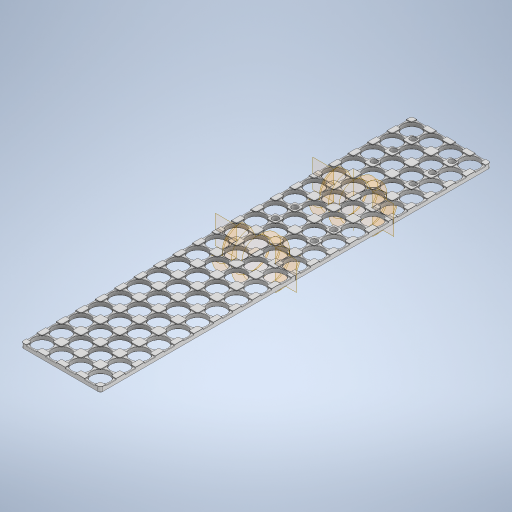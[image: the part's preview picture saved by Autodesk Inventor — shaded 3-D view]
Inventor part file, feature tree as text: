
AUTODESK INVENTOR PART (.ipt)
format: ipt  version: 2024.2 (Build 282272000, 272)  size: 6,418,944 bytes
history: native  units: mm
features: other x22, surface_op x13, chamfer x9, revolve x7, thicken_offset x6, pattern_linear x5, sketch x5, extrude x3, fillet x3, hole x2, split x2, pattern_circular x1
ambient origin geometry x8: Origin, YZ Plane, XZ Plane, XY Plane, X Axis, Y Axis, Z Axis, Center Point
bodies: Solid1 (feature_tree), Solid2 (feature_tree), Solid4 (feature_tree)
feature tree (78):
  extrude  "Extrusion1"  Depth=23.5mm
  extrude  "Extrusion2"  Depth=5.5mm TaperAngle=0.0deg
  fillet  "Fillet1"  Radius=5.5mm
  chamfer  "Chamfer1"  Distance=1.0mm
  chamfer  "Chamfer2"  Distance=0.4mm Angle=45.0deg
  pattern_linear  "Rectangular Pattern1"  Count1=4 Spacing1=23.5mm
  sketch  "Sketch3"  dims[d6=5.5mm d7=1.0mm d8=0.0mm]
  surface_op  "Stitch Surface1"
  other  "Work Axis1"
  pattern_circular  "Circular Pattern1"  Count=20  [1 undecoded]
  surface_op  "Extend3"
  surface_op  "Extend4"
  surface_op  "Stitch Surface8"
  pattern_linear  "Rectangular Pattern2"  Spacing1=23.5mm  [1 undecoded]
  hole  "Hole1"  [1 undecoded]
  chamfer  "Chamfer3"  Distance=23.5mm
  hole  "Hole2"  [1 undecoded]
  chamfer  "Chamfer4"  Distance=13.0mm
  pattern_linear  "Rectangular Pattern4"  Count1=2 Spacing1=23.5mm
  pattern_linear  "Rectangular Pattern5"  Spacing1=10.0mm  [1 undecoded]
  chamfer  "Chamfer5"  Distance=23.5mm
  chamfer  "Chamfer6"  Angle=180.0deg  [1 undecoded]
  thicken_offset  "Thicken8"
  fillet  "Fillet2"  [1 undecoded]
  chamfer  "Chamfer7"  Angle=180.0deg  [1 undecoded]
  chamfer  "Chamfer8"  Angle=180.0deg  [1 undecoded]
  chamfer  "Chamfer9"  Angle=90.0deg  [1 undecoded]
  split  "Split1"
  thicken_offset  "Thicken3"
  thicken_offset  "Thicken4"
  pattern_linear  "Rectangular Pattern6"  Spacing1=90.0deg  [1 undecoded]
  surface_op  "Stitch Surface11"
  split  "Split2"
  thicken_offset  "Thicken5"
  thicken_offset  "Thicken6"
  thicken_offset  "Thicken7"
  fillet  "Fillet3"  [1 undecoded]
  sketch  "Sketch1"  dims[d0=23.5mm d1=23.5mm]
  sketch  "Sketch2"  dims[d2=21.7mm d3=5.0mm d4=0.0mm d5=5.5mm]
  other  "Srf1"
  other  "Srf2"
  other  "Srf3"
  other  "Srf4"
  other  "Srf5"
  other  "Srf6"
  other  "Srf7"
  other  "Srf8"
  other  "Srf9"
  other  "Srf10"
  other  "Srf11"
  other  "Srf12"
  other  "Srf14"
  other  "Srf13"
  other  "Srf15"
  other  "Srf17"
  sketch  "Sketch4"  dims[d9=2.0mm d10=0.4mm d11=2.0mm d12=45.0deg]
  sketch  "Sketch5"  dims[d13=0.2mm d14=2.0mm d15=45.0deg d16=40.0mm d18=23.5mm d19=200.0mm d21=23.5mm d22=23.5mm d23=23.5mm d27=23.5mm d29=45.0deg d30=13.0mm d31=20.0mm d33=23.5mm d34=10.0mm d36=23.5mm d39=23.5mm d41=180.0deg d42=90.0deg d43=180.0deg d44=180.0deg d45=90.0deg d46=90.0deg d47=90.0deg d48=34.0mm d49=0.0mm d50=20.0mm d51=360.0deg d59=30.0mm d61=117.5mm d64=6.756mm d65=6.0mm d66=12.878mm d67=2.0mm d68=14.3117mm d69=8.0mm d70=0.0mm d71=0.5mm d72=2.0mm d73=45.0deg d80=6.756mm d81=6.0mm d82=4.0mm d83=2.0mm d84=90.0deg d85=8.0mm d86=0.0mm d87=0.5mm d88=2.0mm d89=45.0deg d90=20.0mm d92=47.0mm d93=20.0mm d95=23.5mm d96=30.0mm d98=23.5mm d99=20.0mm d101=47.0mm d102=0.5mm d103=2.0mm d104=45.0deg d105=0.5mm d106=2.0mm d107=45.0deg d108=0.3mm d109=0.3mm d110=0.3mm d111=0.3mm d112=20.0mm d114=117.5mm d115=0.3mm d116=0.3mm d117=0.3mm d118=0.3mm d119=0.3mm d120=0.3mm d121=1.0mm d122=1.0mm d123=2.0mm d124=2.0mm d125=0.5mm d126=2.0mm d127=45.0deg d128=0.2mm d129=2.0mm d130=45.0deg d131=0.5mm d132=2.0mm d133=45.0deg d134=3.0mm d135=1.25mm]
  other  "Srf18"
  other  "Srf19"
  other  "Srf20"
  revolve  "RevolutionSrf1"  [1 undecoded]
  revolve  "RevolutionSrf2"  [1 undecoded]
  revolve  "RevolutionSrf3"  Angle=360.0deg
  revolve  "RevolutionSrf4"  [1 undecoded]
  revolve  "RevolutionSrf5"  Angle=45.0deg
  revolve  "RevolutionSrf6"  Angle=45.0deg
  revolve  "RevolutionSrf7"  [1 undecoded]
  extrude  "ExtrusionSrf1"  Depth=23.5mm
  surface_op  "Stitch Surface2"
  surface_op  "Stitch Surface3"
  surface_op  "Stitch Surface4"
  surface_op  "Stitch Surface5"
  surface_op  "Stitch Surface6"
  other  "End"
  surface_op  "Stitch Surface9"
  surface_op  "Stitch Surface10"
  other  "Middle"
  surface_op  "Boundary Patch1"
note: 16 required parameter values undecoded (feature->parameter linkage not recoverable at this tier; creation-order binding heuristic only, values carry confidence <= 0.55)